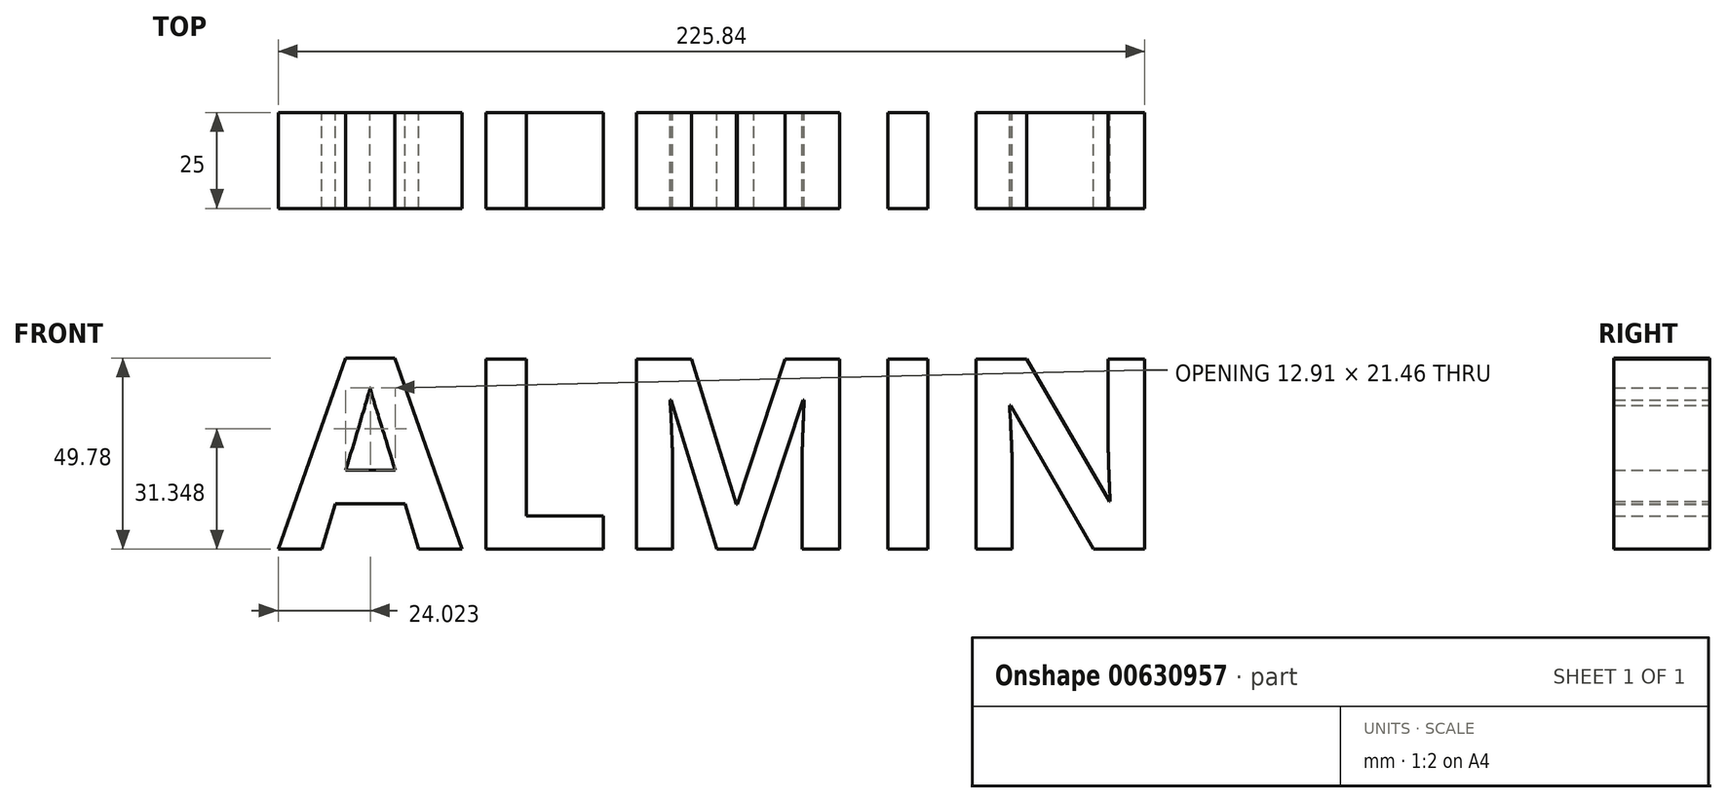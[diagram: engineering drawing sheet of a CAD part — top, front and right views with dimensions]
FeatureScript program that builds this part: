
annotation { "Feature Type Name" : "Feature", "Feature Type Description" : "" }
export const myFeature = defineFeature(function(context is Context, id is Id, definition is map)
    precondition{}
    {
        {
            var Q0;
            Q0=qCreatedBy(makeId("Front.planeOp"),FACE);
            var sketch = newSketch(context, id + "F0", { "sketchPlane" : qUnion([Q0])});
            skText(sketch, "E0", { "text": "ALMIN", "fontName": "OpenSans-Bold.ttf"});
            const initialGuessF0  = {"E0": [-0.09718, -0.01582, 1, 0, 0.05]};
            skSetInitialGuess(sketch, initialGuessF0);
            skSolve(sketch);
        }
        {
            var Q0;
            Q0 = qSketchRegion(id + "F0", true);
            extrude(context, id + "F1", {"entities" : qUnion([Q0]), "depth" : 25 * mm, "offsetDistance" : 25 * mm});
        }
    });
